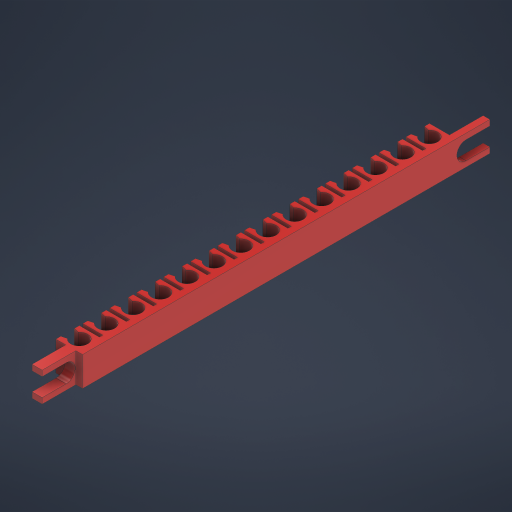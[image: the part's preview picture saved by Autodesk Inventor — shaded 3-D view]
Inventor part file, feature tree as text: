
AUTODESK INVENTOR PART (.ipt)
format: ipt  version: 2024 (Build 280153000, 153)  size: 440,320 bytes
history: native  units: in
note: dims shown in document units (in); Inventor stores cm internally (conversion verified against a paired STEP export)
features: extrude x2, sketch x2
ambient origin geometry x8: Origin, YZ Plane, XZ Plane, XY Plane, X Axis, Y Axis, Z Axis, Center Point
bodies: Solid1 (feature_tree)
feature tree (4):
  extrude  "Extrusion1"  Depth=0.2975in
  extrude  "Extrusion2"  Depth=0.125in
  sketch  "Sketch1"  dims[d1=0.2975in d5=0.7146in]
  sketch  "Sketch3"  dims[d6=0.7146in d7=0.125in d8=0.08in d9=0.1in d10=0.05in d11=0.35in d12=0.075in d14=5.5118in d16=0.4in d17=0.3937in d19=1.0in d21=0.4375in d22=0.0in d25=5.6in d26=2.8in d27=0.5in d28=0.15in d29=0.1in d41=0.5in d45=0.4375in d46=0.2188in d47=0.355in d48=0.355in d49=0.27in d50=0.27in d51=0.0in d52=0.0in]
